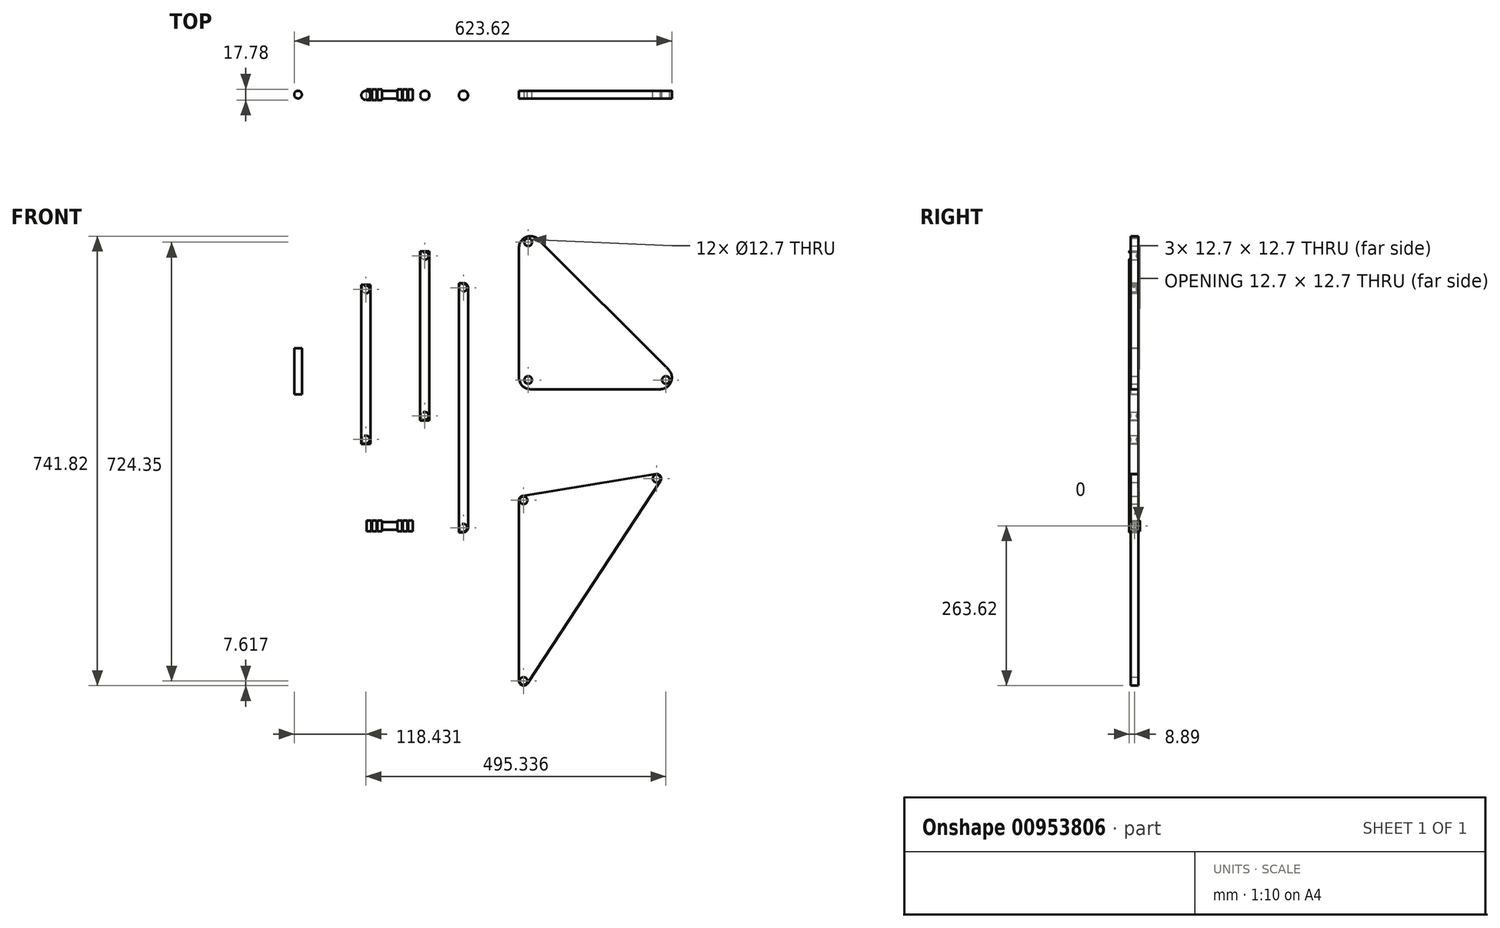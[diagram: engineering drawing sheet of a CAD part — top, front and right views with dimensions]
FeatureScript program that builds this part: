
annotation { "Feature Type Name" : "Feature", "Feature Type Description" : "" }
export const myFeature = defineFeature(function(context is Context, id is Id, definition is map)
    precondition{}
    {
        {
            var Q0;
            Q0=qCreatedBy(makeId("Front.planeOp"),FACE);
            var sketch = newSketch(context, id + "F0", { "sketchPlane" : qUnion([Q0])});
            skLineSegment(sketch, "E0", {"start": v(0, 0) * mm, "end": v(0, 279.4) * mm});
            skLineSegment(sketch, "E1", {"start": v(0, 279.4) * mm, "end": v(279.4, 0) * mm});
            skLineSegment(sketch, "E2", {"start": v(279.4, 0) * mm, "end": v(0, 0) * mm});
            skSolve(sketch);
        }
        {
            var Q0;
            Q0=makeQuery(id+"F0.imprint","IMPRINT",FACE,{"disambiguationData":[TD([[makeQuery(id+"F0.imprint","IMPRINT",EDGE,{"derivedFrom":sQuery(id+"F0.wireOp",EDGE,"E0")}),-1.0]])]});
            extrude(context, id + "F1", {"entities" : qUnion([Q0]), "depth" : 12.7 * mm, "offsetDistance" : 25.4 * mm});
        }
        {
            var Q0;
            Q0=makeQuery(id+"F1.opExtrude","CAP_FACE",FACE,{"disambiguationData":[OSD([sQuery(id+"F0.wireOp",EDGE,"E0"),sQuery(id+"F0.wireOp",EDGE,"E1"),sQuery(id+"F0.wireOp",EDGE,"E2")])],"isStart":true});
            var sketch = newSketch(context, id + "F2", { "sketchPlane" : qUnion([Q0])});
            skPoint(sketch, "E3", {"position": v(-242.6, 15.24) * mm});
            skPoint(sketch, "E4", {"position": v(-15.24, 15.24) * mm});
            skPoint(sketch, "E5", {"position": v(-15.24, 242.6) * mm});
            skLineSegment(sketch, "E6", {"start": v(0, -112.73) * mm, "end": v(-246.38, -112.73) * mm});
            skLineSegment(sketch, "E7", {"start": v(-246.38, -112.73) * mm, "end": v(51.94, -438.82) * mm});
            skLineSegment(sketch, "E8", {"start": v(51.94, -438.82) * mm, "end": v(0, -112.73) * mm});
            skSolve(sketch);
        }
        {
            var Q0;
            Q0=sQuery(id+"F2.wireOp",VERTEX,"E3");
            var Q1;
            Q1=sQuery(id+"F2.wireOp",VERTEX,"E4");
            var Q2;
            Q2=sQuery(id+"F2.wireOp",VERTEX,"E5");
            var Q3;
            Q3=makeQuery(id+"F1.opExtrude","SWEPT_BODY",BODY,{"disambiguationData":[OSD([sQuery(id+"F0.wireOp",EDGE,"E0"),sQuery(id+"F0.wireOp",EDGE,"E1"),sQuery(id+"F0.wireOp",EDGE,"E2")])]});
            hole(context, id + "F3", {"style" : HoleStyle.SIMPLE, "endStyle" : HoleEndStyle.THROUGH, "holeDiameter" : 12.7 * mm, "majorDiameter" : 6.35 * mm, "isTappedThrough" : true, "tappedDepth" : 12.7 * mm, "tapClearance" : 3, "locations" : qUnion([Q0, Q1, Q2]), "scope" : qUnion([Q3])});
        }
        {
            var Q0;
            Q0=makeQuery(id+"F1.opExtrude","SWEPT_EDGE",EDGE,{"disambiguationData":[OSD([sQuery(id+"F0.wireOp",EDGE,"E0"),sQuery(id+"F0.wireOp",EDGE,"E2")])]});
            var Q1;
            Q1=makeQuery(id+"F1.opExtrude","SWEPT_EDGE",EDGE,{"disambiguationData":[OSD([sQuery(id+"F0.wireOp",EDGE,"E0"),sQuery(id+"F0.wireOp",EDGE,"E1")])]});
            var Q2;
            Q2=makeQuery(id+"F1.opExtrude","SWEPT_EDGE",EDGE,{"disambiguationData":[OSD([sQuery(id+"F0.wireOp",EDGE,"E1"),sQuery(id+"F0.wireOp",EDGE,"E2")])]});
            fillet(context, id + "F4", {"entities" : qUnion([Q0, Q1, Q2]), "radius" : 19.05 * mm, "tangentPropagation" : true, "allowEdgeOverflow" : false});
        }
        {
            var Q0;
            Q0=qCreatedBy(makeId("Front.planeOp"),FACE);
            var sketch = newSketch(context, id + "F5", { "sketchPlane" : qUnion([Q0])});
            skLineSegment(sketch, "E9.bottom", {"start": v(-163, 227.77) * mm, "end": v(-147.77, 227.77) * mm});
            skLineSegment(sketch, "E9.top", {"start": v(-163, -51.63) * mm, "end": v(-147.77, -51.63) * mm});
            skLineSegment(sketch, "E9.left", {"start": v(-163, 227.77) * mm, "end": v(-163, -51.63) * mm});
            skLineSegment(sketch, "E9.right", {"start": v(-147.77, 227.77) * mm, "end": v(-147.77, -51.63) * mm});
            skLineSegment(sketch, "E10", {"start": v(-163, 212.53) * mm, "end": v(-147.77, 212.53) * mm, "construction": true});
            skLineSegment(sketch, "E11", {"start": v(-155.39, 227.77) * mm, "end": v(-155.39, 212.53) * mm, "construction": true});
            skLineSegment(sketch, "E12", {"start": v(-155.39, 220.15) * mm, "end": v(-163, 220.15) * mm, "construction": true});
            skLineSegment(sketch, "E13", {"start": v(-155.39, 220.15) * mm, "end": v(-147.77, 220.15) * mm, "construction": true});
            skLineSegment(sketch, "E14", {"start": v(-163, -36.39) * mm, "end": v(-147.77, -36.39) * mm, "construction": true});
            skLineSegment(sketch, "E15", {"start": v(-155.39, -36.39) * mm, "end": v(-155.39, -51.63) * mm, "construction": true});
            skLineSegment(sketch, "E16", {"start": v(-155.39, -44) * mm, "end": v(-147.77, -44) * mm, "construction": true});
            skLineSegment(sketch, "E17", {"start": v(-147.77, -44) * mm, "end": v(-155.39, -44) * mm, "construction": true});
            skLineSegment(sketch, "E18", {"start": v(-163, -44) * mm, "end": v(-155.39, -44) * mm, "construction": true});
            skCircle(sketch, "E19", {"center": v(-155.39, -44) * mm, "radius": 6.35 * mm});
            skCircle(sketch, "E20", {"center": v(-155.39, 220.15) * mm, "radius": 6.35 * mm});
            skSolve(sketch);
        }
        {
            var Q0;
            Q0=makeQuery(id+"F5.imprint","IMPRINT",FACE,{"disambiguationData":[TD([[makeQuery(id+"F5.imprint","IMPRINT",EDGE,{"derivedFrom":sQuery(id+"F5.wireOp",EDGE,"E9.bottom")}),-1.0]])]});
            extrude(context, id + "F6", {"entities" : qUnion([Q0]), "depth" : 15.24 * mm, "offsetDistance" : 25.4 * mm});
        }
        {
            var Q0;
            Q0=makeQuery(id+"F6.opExtrude","CAP_EDGE",EDGE,{"disambiguationData":[OSD([sQuery(id+"F5.wireOp",EDGE,"E9.left")])],"isStart":false});
            var Q1;
            Q1=makeQuery(id+"F6.opExtrude","CAP_EDGE",EDGE,{"disambiguationData":[OSD([sQuery(id+"F5.wireOp",EDGE,"E9.right")])],"isStart":false});
            var Q2;
            Q2=makeQuery(id+"F6.opExtrude","CAP_EDGE",EDGE,{"disambiguationData":[OSD([sQuery(id+"F5.wireOp",EDGE,"E9.right")])],"isStart":true});
            var Q3;
            Q3=makeQuery(id+"F6.opExtrude","CAP_EDGE",EDGE,{"disambiguationData":[OSD([sQuery(id+"F5.wireOp",EDGE,"E9.left")])],"isStart":true});
            fillet(context, id + "F7", {"entities" : qUnion([Q0, Q1, Q2, Q3]), "radius" : 7.62 * mm, "tangentPropagation" : true, "allowEdgeOverflow" : false});
        }
        {
            var Q0;
            Q0=qCreatedBy(makeId("Front.planeOp"),FACE);
            var sketch = newSketch(context, id + "F8", { "sketchPlane" : qUnion([Q0])});
            skLineSegment(sketch, "E21.bottom", {"start": v(-260.35, 172.29) * mm, "end": v(-245.1, 172.29) * mm});
            skLineSegment(sketch, "E21.top", {"start": v(-260.35, -90.6) * mm, "end": v(-245.1, -90.6) * mm});
            skLineSegment(sketch, "E21.left", {"start": v(-260.35, 172.29) * mm, "end": v(-260.35, -90.6) * mm});
            skLineSegment(sketch, "E21.right", {"start": v(-245.1, 172.29) * mm, "end": v(-245.1, -90.6) * mm});
            skLineSegment(sketch, "E22", {"start": v(-260.35, 157.05) * mm, "end": v(-245.1, 157.05) * mm, "construction": true});
            skLineSegment(sketch, "E23", {"start": v(-252.73, 172.29) * mm, "end": v(-252.73, 157.05) * mm, "construction": true});
            skLineSegment(sketch, "E24", {"start": v(-252.73, 157.05) * mm, "end": v(-252.73, 164.67) * mm, "construction": true});
            skLineSegment(sketch, "E25", {"start": v(-252.73, 164.67) * mm, "end": v(-260.35, 164.67) * mm, "construction": true});
            skLineSegment(sketch, "E26", {"start": v(-260.35, 164.67) * mm, "end": v(-252.73, 164.67) * mm, "construction": true});
            skLineSegment(sketch, "E27", {"start": v(-245.1, 164.67) * mm, "end": v(-252.73, 164.67) * mm, "construction": true});
            skLineSegment(sketch, "E28", {"start": v(-260.35, -75.36) * mm, "end": v(-245.1, -75.36) * mm, "construction": true});
            skLineSegment(sketch, "E29", {"start": v(-252.73, -75.36) * mm, "end": v(-252.73, -90.6) * mm, "construction": true});
            skLineSegment(sketch, "E30", {"start": v(-252.73, -90.6) * mm, "end": v(-252.73, -82.98) * mm, "construction": true});
            skLineSegment(sketch, "E31", {"start": v(-252.73, -82.98) * mm, "end": v(-260.35, -82.98) * mm, "construction": true});
            skLineSegment(sketch, "E32", {"start": v(-260.35, -82.98) * mm, "end": v(-252.73, -82.98) * mm, "construction": true});
            skLineSegment(sketch, "E33", {"start": v(-245.1, -82.98) * mm, "end": v(-252.73, -82.98) * mm, "construction": true});
            skCircle(sketch, "E34", {"center": v(-252.73, -82.98) * mm, "radius": 6.35 * mm});
            skCircle(sketch, "E35", {"center": v(-252.73, 164.67) * mm, "radius": 6.35 * mm});
            skSolve(sketch);
        }
        {
            var Q0;
            Q0=makeQuery(id+"F8.imprint","IMPRINT",FACE,{"disambiguationData":[TD([[makeQuery(id+"F8.imprint","IMPRINT",EDGE,{"derivedFrom":sQuery(id+"F8.wireOp",EDGE,"E21.bottom")}),-1.0]])]});
            extrude(context, id + "F9", {"entities" : qUnion([Q0]), "depth" : 15.24 * mm, "offsetDistance" : 25.4 * mm});
        }
        {
            var Q0;
            Q0=makeQuery(id+"F9.opExtrude","CAP_EDGE",EDGE,{"disambiguationData":[OSD([sQuery(id+"F8.wireOp",EDGE,"E21.left")])],"isStart":false});
            var Q1;
            Q1=makeQuery(id+"F9.opExtrude","CAP_EDGE",EDGE,{"disambiguationData":[OSD([sQuery(id+"F8.wireOp",EDGE,"E21.right")])],"isStart":false});
            var Q2;
            Q2=makeQuery(id+"F9.opExtrude","CAP_EDGE",EDGE,{"disambiguationData":[OSD([sQuery(id+"F8.wireOp",EDGE,"E21.left")])],"isStart":true});
            var Q3;
            Q3=makeQuery(id+"F9.opExtrude","CAP_EDGE",EDGE,{"disambiguationData":[OSD([sQuery(id+"F8.wireOp",EDGE,"E21.right")])],"isStart":true});
            fillet(context, id + "F10", {"entities" : qUnion([Q0, Q1, Q2, Q3]), "radius" : 7.62 * mm, "tangentPropagation" : true, "allowEdgeOverflow" : false});
        }
        {
            var Q0;
            Q0=qCreatedBy(makeId("Front.planeOp"),FACE);
            var sketch = newSketch(context, id + "F11", { "sketchPlane" : qUnion([Q0])});
            skLineSegment(sketch, "E36", {"start": v(0, -177.01) * mm, "end": v(0, -507.21) * mm});
            skLineSegment(sketch, "E37", {"start": v(0, -507.21) * mm, "end": v(243.15, -137.24) * mm});
            skLineSegment(sketch, "E38", {"start": v(243.15, -137.24) * mm, "end": v(0, -177.01) * mm});
            skPoint(sketch, "E39", {"position": v(7.62, -183.49) * mm});
            skPoint(sketch, "E40", {"position": v(227.25, -147.56) * mm});
            skCircle(sketch, "E41", {"center": v(7.62, -183.49) * mm, "radius": 6.35 * mm});
            skCircle(sketch, "E42", {"center": v(227.25, -147.56) * mm, "radius": 6.35 * mm});
            skPoint(sketch, "E43", {"position": v(7.62, -481.74) * mm});
            skCircle(sketch, "E44", {"center": v(7.62, -481.74) * mm, "radius": 6.35 * mm});
            skSolve(sketch);
        }
        {
            var Q0;
            Q0=makeQuery(id+"F11.imprint","IMPRINT",FACE,{"disambiguationData":[TD([[makeQuery(id+"F11.imprint","IMPRINT",EDGE,{"derivedFrom":sQuery(id+"F11.wireOp",EDGE,"E36")}),1.0]])]});
            extrude(context, id + "F12", {"entities" : qUnion([Q0]), "depth" : 12.7 * mm, "offsetDistance" : 25.4 * mm});
        }
        {
            var Q0;
            Q0=makeQuery(id+"F12.opExtrude","SWEPT_EDGE",EDGE,{"disambiguationData":[OSD([sQuery(id+"F11.wireOp",EDGE,"E37"),sQuery(id+"F11.wireOp",EDGE,"E38")])]});
            var Q1;
            Q1=makeQuery(id+"F12.opExtrude","SWEPT_EDGE",EDGE,{"disambiguationData":[OSD([sQuery(id+"F11.wireOp",EDGE,"E36"),sQuery(id+"F11.wireOp",EDGE,"E37")])]});
            var Q2;
            Q2=makeQuery(id+"F12.opExtrude","SWEPT_EDGE",EDGE,{"disambiguationData":[OSD([sQuery(id+"F11.wireOp",EDGE,"E36"),sQuery(id+"F11.wireOp",EDGE,"E38")])]});
            fillet(context, id + "F13", {"entities" : qUnion([Q0, Q1, Q2]), "radius" : 7.62 * mm, "tangentPropagation" : true, "allowEdgeOverflow" : false});
        }
        {
            var Q0;
            Q0=qCreatedBy(makeId("Front.planeOp"),FACE);
            var sketch = newSketch(context, id + "F14", { "sketchPlane" : qUnion([Q0])});
            skLineSegment(sketch, "E45.bottom", {"start": v(-251.68, -219.4) * mm, "end": v(-175.48, -219.4) * mm});
            skLineSegment(sketch, "E45.top", {"start": v(-251.68, -232.1) * mm, "end": v(-175.48, -232.1) * mm});
            skLineSegment(sketch, "E45.left", {"start": v(-251.68, -219.4) * mm, "end": v(-251.68, -232.1) * mm});
            skLineSegment(sketch, "E45.right", {"start": v(-175.48, -219.4) * mm, "end": v(-175.48, -232.1) * mm});
            skSolve(sketch);
        }
        {
            var Q0;
            Q0=makeQuery(id+"F14.imprint","IMPRINT",FACE,{"disambiguationData":[TD([[makeQuery(id+"F14.imprint","IMPRINT",EDGE,{"derivedFrom":sQuery(id+"F14.wireOp",EDGE,"E45.bottom")}),-1.0]])]});
            extrude(context, id + "F15", {"entities" : qUnion([Q0]), "depth" : 12.7 * mm, "offsetDistance" : 25.4 * mm});
        }
        {
            var Q0;
            Q0=makeQuery(id+"F15.opExtrude","CAP_FACE",FACE,{"disambiguationData":[OSD([sQuery(id+"F14.wireOp",EDGE,"E45.bottom"),sQuery(id+"F14.wireOp",EDGE,"E45.top"),sQuery(id+"F14.wireOp",EDGE,"E45.left"),sQuery(id+"F14.wireOp",EDGE,"E45.right")])],"isStart":false});
            var sketch = newSketch(context, id + "F16", { "sketchPlane" : qUnion([Q0])});
            skLineSegment(sketch, "E46", {"start": v(-213.58, -219.4) * mm, "end": v(-213.58, -232.1) * mm});
            skLineSegment(sketch, "E47", {"start": v(-226.28, -219.4) * mm, "end": v(-226.28, -232.1) * mm});
            skLineSegment(sketch, "E48", {"start": v(-200.88, -232.1) * mm, "end": v(-200.88, -219.4) * mm});
            skLineSegment(sketch, "E49.bottom", {"start": v(-193.26, -219.4) * mm, "end": v(-191.99, -219.4) * mm});
            skLineSegment(sketch, "E49.top", {"start": v(-193.26, -232.1) * mm, "end": v(-191.99, -232.1) * mm});
            skLineSegment(sketch, "E49.left", {"start": v(-193.26, -219.4) * mm, "end": v(-193.26, -232.1) * mm});
            skLineSegment(sketch, "E49.right", {"start": v(-191.99, -219.4) * mm, "end": v(-191.99, -232.1) * mm});
            skLineSegment(sketch, "E50.bottom", {"start": v(-184.37, -219.4) * mm, "end": v(-183.1, -219.4) * mm});
            skLineSegment(sketch, "E50.top", {"start": v(-184.37, -232.1) * mm, "end": v(-183.1, -232.1) * mm});
            skLineSegment(sketch, "E50.left", {"start": v(-184.37, -219.4) * mm, "end": v(-184.37, -232.1) * mm});
            skLineSegment(sketch, "E50.right", {"start": v(-183.1, -219.4) * mm, "end": v(-183.1, -232.1) * mm});
            skLineSegment(sketch, "E51.bottom", {"start": v(-244.06, -219.4) * mm, "end": v(-242.79, -219.4) * mm});
            skLineSegment(sketch, "E51.top", {"start": v(-244.06, -232.1) * mm, "end": v(-242.79, -232.1) * mm});
            skLineSegment(sketch, "E51.left", {"start": v(-244.06, -219.4) * mm, "end": v(-244.06, -232.1) * mm});
            skLineSegment(sketch, "E51.right", {"start": v(-242.79, -219.4) * mm, "end": v(-242.79, -232.1) * mm});
            skLineSegment(sketch, "E52.bottom", {"start": v(-235.17, -219.4) * mm, "end": v(-233.9, -219.4) * mm});
            skLineSegment(sketch, "E52.top", {"start": v(-235.17, -232.1) * mm, "end": v(-233.9, -232.1) * mm});
            skLineSegment(sketch, "E52.left", {"start": v(-235.17, -219.4) * mm, "end": v(-235.17, -232.1) * mm});
            skLineSegment(sketch, "E52.right", {"start": v(-233.9, -219.4) * mm, "end": v(-233.9, -232.1) * mm});
            skSolve(sketch);
        }
        {
            var Q0;
            {var subQ0=sQuery(id+"F16.wireOp",EDGE,"E51.left");Q0=makeQuery(id+"F16.imprint","IMPRINT",FACE,{"disambiguationData":[TD([[makeQuery(id+"F16.imprint","IMPRINT",EDGE,{"derivedFrom":subQ0}),-1.0]])]});}
            var Q1;
            {var subQ0=sQuery(id+"F16.wireOp",EDGE,"E51.right");Q1=makeQuery(id+"F16.imprint","IMPRINT",FACE,{"disambiguationData":[TD([[makeQuery(id+"F16.imprint","IMPRINT",EDGE,{"derivedFrom":subQ0}),1.0]])]});}
            var Q2;
            {var subQ0=sQuery(id+"F16.wireOp",EDGE,"E47");Q2=makeQuery(id+"F16.imprint","IMPRINT",FACE,{"disambiguationData":[TD([[makeQuery(id+"F16.imprint","IMPRINT",EDGE,{"derivedFrom":subQ0}),-1.0]])]});}
            var Q3;
            {var subQ0=sQuery(id+"F16.wireOp",EDGE,"E48");Q3=makeQuery(id+"F16.imprint","IMPRINT",FACE,{"disambiguationData":[TD([[makeQuery(id+"F16.imprint","IMPRINT",EDGE,{"derivedFrom":subQ0}),-1.0]])]});}
            var Q4;
            {var subQ0=sQuery(id+"F16.wireOp",EDGE,"E49.right");Q4=makeQuery(id+"F16.imprint","IMPRINT",FACE,{"disambiguationData":[TD([[makeQuery(id+"F16.imprint","IMPRINT",EDGE,{"derivedFrom":subQ0}),1.0]])]});}
            var Q5;
            {var subQ0=sQuery(id+"F16.wireOp",EDGE,"E50.right");Q5=makeQuery(id+"F16.imprint","IMPRINT",FACE,{"disambiguationData":[TD([[makeQuery(id+"F16.imprint","IMPRINT",EDGE,{"derivedFrom":subQ0}),1.0]])]});}
            extrude(context, id + "F17", {"entities" : qUnion([Q0, Q1, Q2, Q3, Q4, Q5]), "operationType" : NewBodyOperationType.ADD, "depth" : 2.54 * mm, "offsetDistance" : 25.4 * mm, "hasSecondDirection" : true, "secondDirectionOppositeDirection" : true, "secondDirectionDepth" : 15.24 * mm});
        }
        {
            var Q0;
            {var subQ0=sQuery(id+"F16.wireOp",EDGE,"E51.bottom");var subQ1=sQuery(id+"F14.wireOp",EDGE,"E45.bottom");var subQ2=makeQuery(id+"F15.opExtrude","CAP_EDGE",EDGE,{"disambiguationData":[OSD([subQ1])],"isStart":false});var subQ4=sQuery(id+"F16.wireOp",EDGE,"E49.bottom");Q0=makeQuery(id+"F17.boolean.opBoolean","MERGE",FACE,{"derivedFrom":[makeQuery(id+"F15.opExtrude","SWEPT_FACE",FACE,{"disambiguationData":[OSD([subQ1])]}),makeQuery(id+"F17.opExtrude","SWEPT_FACE",FACE,{"disambiguationData":[OSD([subQ1]),TDD([makeQuery(id+"F16.imprint","IMPRINT",EDGE,{"disambiguationData":[TD([[makeQuery(id+"F16.imprint","INTERSECT",VERTEX,{"derivedFrom":[subQ2,makeQuery(id+"F15.opExtrude","CAP_EDGE",EDGE,{"disambiguationData":[OSD([sQuery(id+"F14.wireOp",EDGE,"E45.left")])],"isStart":false})]}),-1.0]])],"derivedFrom":subQ2})])]}),makeQuery(id+"F17.opExtrude","SWEPT_FACE",FACE,{"disambiguationData":[OSD([subQ1]),TDD([makeQuery(id+"F16.imprint","IMPRINT",EDGE,{"disambiguationData":[TD([[makeQuery(id+"F16.imprint","INTERSECT",VERTEX,{"derivedFrom":[subQ2,makeQuery(id+"F15.opExtrude","CAP_EDGE",EDGE,{"disambiguationData":[OSD([sQuery(id+"F14.wireOp",EDGE,"E45.right")])],"isStart":false})]}),1.0]])],"derivedFrom":subQ2})])]}),makeQuery(id+"F17.opExtrude","SWEPT_FACE",FACE,{"disambiguationData":[OSD([subQ1]),TDD([makeQuery(id+"F16.imprint","IMPRINT",EDGE,{"disambiguationData":[TD([[makeQuery(id+"F16.imprint","INTERSECT",VERTEX,{"derivedFrom":[subQ2,sQuery(id+"F16.wireOp",EDGE,"E47")]}),1.0]])],"derivedFrom":subQ2})])]}),makeQuery(id+"F17.opExtrude","SWEPT_FACE",FACE,{"disambiguationData":[OSD([subQ1]),TDD([makeQuery(id+"F16.imprint","IMPRINT",EDGE,{"disambiguationData":[TD([[makeQuery(id+"F16.imprint","INTERSECT",VERTEX,{"derivedFrom":[subQ2,sQuery(id+"F16.wireOp",EDGE,"E48")]}),-1.0]])],"derivedFrom":subQ2})])]}),makeQuery(id+"F17.opExtrude","SWEPT_FACE",FACE,{"disambiguationData":[OSD([subQ1]),TDD([makeQuery(id+"F16.imprint","IMPRINT",EDGE,{"disambiguationData":[TD([[makeQuery(id+"F16.imprint","INTERSECT",VERTEX,{"derivedFrom":[subQ2,subQ4,sQuery(id+"F16.wireOp",EDGE,"E49.right")]}),-1.0]])],"derivedFrom":subQ2})])]}),makeQuery(id+"F17.opExtrude","SWEPT_FACE",FACE,{"disambiguationData":[OSD([subQ1]),TDD([makeQuery(id+"F16.imprint","IMPRINT",EDGE,{"disambiguationData":[TD([[makeQuery(id+"F16.imprint","INTERSECT",VERTEX,{"derivedFrom":[subQ2,subQ0,sQuery(id+"F16.wireOp",EDGE,"E51.right")]}),-1.0]])],"derivedFrom":subQ2})])]})]});}
            var sketch = newSketch(context, id + "F18", { "sketchPlane" : qUnion([Q0])});
            skLineSegment(sketch, "E53.bottom", {"start": v(-244.06, 0) * mm, "end": v(-242.79, 0) * mm});
            skLineSegment(sketch, "E53.top", {"start": v(-244.06, -12.7) * mm, "end": v(-242.79, -12.7) * mm});
            skLineSegment(sketch, "E53.left", {"start": v(-244.06, 0) * mm, "end": v(-244.06, -12.7) * mm});
            skLineSegment(sketch, "E53.right", {"start": v(-242.79, 0) * mm, "end": v(-242.79, -12.7) * mm});
            skLineSegment(sketch, "E54.bottom", {"start": v(-235.17, 0) * mm, "end": v(-233.9, 0) * mm});
            skLineSegment(sketch, "E54.top", {"start": v(-235.17, -12.7) * mm, "end": v(-233.9, -12.7) * mm});
            skLineSegment(sketch, "E54.left", {"start": v(-235.17, 0) * mm, "end": v(-235.17, -12.7) * mm});
            skLineSegment(sketch, "E54.right", {"start": v(-233.9, 0) * mm, "end": v(-233.9, -12.7) * mm});
            skLineSegment(sketch, "E55.bottom", {"start": v(-193.26, 0) * mm, "end": v(-191.99, 0) * mm});
            skLineSegment(sketch, "E55.top", {"start": v(-193.26, -12.7) * mm, "end": v(-191.99, -12.7) * mm});
            skLineSegment(sketch, "E55.left", {"start": v(-193.26, 0) * mm, "end": v(-193.26, -12.7) * mm});
            skLineSegment(sketch, "E55.right", {"start": v(-191.99, 0) * mm, "end": v(-191.99, -12.7) * mm});
            skLineSegment(sketch, "E56.bottom", {"start": v(-184.37, 0) * mm, "end": v(-183.1, 0) * mm});
            skLineSegment(sketch, "E56.top", {"start": v(-184.37, -12.7) * mm, "end": v(-183.1, -12.7) * mm});
            skLineSegment(sketch, "E56.left", {"start": v(-184.37, 0) * mm, "end": v(-184.37, -12.7) * mm});
            skLineSegment(sketch, "E56.right", {"start": v(-183.1, 0) * mm, "end": v(-183.1, -12.7) * mm});
            skLineSegment(sketch, "E57", {"start": v(-200.88, 0) * mm, "end": v(-200.88, -12.7) * mm});
            skLineSegment(sketch, "E58", {"start": v(-226.28, 0) * mm, "end": v(-226.28, -12.7) * mm});
            skSolve(sketch);
        }
        {
            var Q0;
            Q0=makeQuery(id+"F18.imprint","IMPRINT",FACE,{"disambiguationData":[TD([[makeQuery(id+"F18.imprint","IMPRINT",EDGE,{"derivedFrom":sQuery(id+"F18.wireOp",EDGE,"E53.left")}),-1.0]])]});
            var Q1;
            Q1=makeQuery(id+"F18.imprint","IMPRINT",FACE,{"disambiguationData":[TD([[makeQuery(id+"F18.imprint","IMPRINT",EDGE,{"derivedFrom":sQuery(id+"F18.wireOp",EDGE,"E53.right")}),1.0]])]});
            var Q2;
            Q2=makeQuery(id+"F18.imprint","IMPRINT",FACE,{"disambiguationData":[TD([[makeQuery(id+"F18.imprint","IMPRINT",EDGE,{"derivedFrom":sQuery(id+"F18.wireOp",EDGE,"E54.right")}),1.0]])]});
            var Q3;
            Q3=makeQuery(id+"F18.imprint","IMPRINT",FACE,{"disambiguationData":[TD([[makeQuery(id+"F18.imprint","IMPRINT",EDGE,{"derivedFrom":sQuery(id+"F18.wireOp",EDGE,"E55.left")}),-1.0]])]});
            var Q4;
            Q4=makeQuery(id+"F18.imprint","IMPRINT",FACE,{"disambiguationData":[TD([[makeQuery(id+"F18.imprint","IMPRINT",EDGE,{"derivedFrom":sQuery(id+"F18.wireOp",EDGE,"E55.right")}),1.0]])]});
            var Q5;
            Q5=makeQuery(id+"F18.imprint","IMPRINT",FACE,{"disambiguationData":[TD([[makeQuery(id+"F18.imprint","IMPRINT",EDGE,{"derivedFrom":sQuery(id+"F18.wireOp",EDGE,"E56.right")}),1.0]])]});
            extrude(context, id + "F19", {"entities" : qUnion([Q0, Q1, Q2, Q3, Q4, Q5]), "operationType" : NewBodyOperationType.ADD, "depth" : 2.54 * mm, "offsetDistance" : 25.4 * mm, "hasSecondDirection" : true, "secondDirectionOppositeDirection" : true, "secondDirectionDepth" : 15.24 * mm});
        }
        {
            var Q0;
            {var subQ2=sQuery(id+"F14.wireOp",EDGE,"E45.bottom");var subQ3=makeQuery(id+"F15.opExtrude","CAP_EDGE",EDGE,{"disambiguationData":[OSD([subQ2])],"isStart":false});var subQ5=sQuery(id+"F16.wireOp",EDGE,"E47");Q0=makeQuery(id+"F17.boolean.opBoolean","SPLIT",EDGE,{"disambiguationData":[TD([makeQuery(id+"F17.opExtrude","SWEPT_FACE",FACE,{"disambiguationData":[OSD([subQ5])]})])],"derivedFrom":subQ3});}
            var Q1;
            {var subQ1=sQuery(id+"F16.wireOp",EDGE,"E47");var subQ2=sQuery(id+"F14.wireOp",EDGE,"E45.top");var subQ3=makeQuery(id+"F15.opExtrude","CAP_EDGE",EDGE,{"disambiguationData":[OSD([subQ2])],"isStart":false});Q1=makeQuery(id+"F17.boolean.opBoolean","SPLIT",EDGE,{"disambiguationData":[TD([makeQuery(id+"F17.opExtrude","SWEPT_FACE",FACE,{"disambiguationData":[OSD([subQ1])]})])],"derivedFrom":subQ3});}
            var Q2;
            {var subQ0=sQuery(id+"F16.wireOp",EDGE,"E47");var subQ3=sQuery(id+"F14.wireOp",EDGE,"E45.top");Q2=makeQuery(id+"F17.boolean.opBoolean","SPLIT",EDGE,{"disambiguationData":[TD([makeQuery(id+"F17.opExtrude","SWEPT_FACE",FACE,{"disambiguationData":[OSD([subQ0])]})])],"derivedFrom":makeQuery(id+"F15.opExtrude","CAP_EDGE",EDGE,{"disambiguationData":[OSD([subQ3])],"isStart":true})});}
            var Q3;
            {var subQ0=sQuery(id+"F16.wireOp",EDGE,"E47");var subQ3=sQuery(id+"F14.wireOp",EDGE,"E45.bottom");Q3=makeQuery(id+"F17.boolean.opBoolean","SPLIT",EDGE,{"disambiguationData":[TD([makeQuery(id+"F17.opExtrude","SWEPT_FACE",FACE,{"disambiguationData":[OSD([subQ0])]})])],"derivedFrom":makeQuery(id+"F15.opExtrude","CAP_EDGE",EDGE,{"disambiguationData":[OSD([subQ3])],"isStart":true})});}
            fillet(context, id + "F20", {"entities" : qUnion([Q0, Q1, Q2, Q3]), "radius" : 6.35 * mm, "tangentPropagation" : true, "allowEdgeOverflow" : false});
        }
        {
            var Q0;
            Q0=qCreatedBy(makeId("Front.planeOp"),FACE);
            var sketch = newSketch(context, id + "F21", { "sketchPlane" : qUnion([Q0])});
            skLineSegment(sketch, "E59.bottom", {"start": v(-371.16, 67.4) * mm, "end": v(-358.46, 67.4) * mm});
            skLineSegment(sketch, "E59.top", {"start": v(-371.16, -8.8) * mm, "end": v(-358.46, -8.8) * mm});
            skLineSegment(sketch, "E59.left", {"start": v(-371.16, 67.4) * mm, "end": v(-371.16, -8.8) * mm});
            skLineSegment(sketch, "E59.right", {"start": v(-358.46, 67.4) * mm, "end": v(-358.46, -8.8) * mm});
            skSolve(sketch);
        }
        {
            var Q0;
            Q0=makeQuery(id+"F21.imprint","IMPRINT",FACE,{"disambiguationData":[TD([[makeQuery(id+"F21.imprint","IMPRINT",EDGE,{"derivedFrom":sQuery(id+"F21.wireOp",EDGE,"E59.bottom")}),-1.0]])]});
            extrude(context, id + "F22", {"entities" : qUnion([Q0]), "depth" : 12.7 * mm, "offsetDistance" : 25.4 * mm});
        }
        {
            var Q0;
            Q0=makeQuery(id+"F22.opExtrude","CAP_EDGE",EDGE,{"disambiguationData":[OSD([sQuery(id+"F21.wireOp",EDGE,"E59.left")])],"isStart":false});
            var Q1;
            Q1=makeQuery(id+"F22.opExtrude","CAP_EDGE",EDGE,{"disambiguationData":[OSD([sQuery(id+"F21.wireOp",EDGE,"E59.right")])],"isStart":false});
            var Q2;
            Q2=makeQuery(id+"F22.opExtrude","CAP_EDGE",EDGE,{"disambiguationData":[OSD([sQuery(id+"F21.wireOp",EDGE,"E59.right")])],"isStart":true});
            var Q3;
            Q3=makeQuery(id+"F22.opExtrude","CAP_EDGE",EDGE,{"disambiguationData":[OSD([sQuery(id+"F21.wireOp",EDGE,"E59.left")])],"isStart":true});
            fillet(context, id + "F23", {"entities" : qUnion([Q0, Q1, Q2, Q3]), "radius" : 6.35 * mm, "tangentPropagation" : true, "allowEdgeOverflow" : false});
        }
        {
            var Q0;
            Q0=qCreatedBy(makeId("Front.planeOp"),FACE);
            var sketch = newSketch(context, id + "F24", { "sketchPlane" : qUnion([Q0])});
            skLineSegment(sketch, "E60.bottom", {"start": v(-99.33, 175.18) * mm, "end": v(-84.09, 175.18) * mm});
            skLineSegment(sketch, "E60.top", {"start": v(-99.33, -236.3) * mm, "end": v(-84.09, -236.3) * mm});
            skLineSegment(sketch, "E60.left", {"start": v(-99.33, 175.18) * mm, "end": v(-99.33, -236.3) * mm});
            skLineSegment(sketch, "E60.right", {"start": v(-84.09, 175.18) * mm, "end": v(-84.09, -236.3) * mm});
            skLineSegment(sketch, "E61", {"start": v(-99.33, 159.94) * mm, "end": v(-84.09, 159.94) * mm, "construction": true});
            skLineSegment(sketch, "E62", {"start": v(-91.7, 175.18) * mm, "end": v(-91.7, 159.94) * mm, "construction": true});
            skLineSegment(sketch, "E63", {"start": v(-91.7, 159.94) * mm, "end": v(-91.7, 167.56) * mm, "construction": true});
            skLineSegment(sketch, "E64", {"start": v(-91.7, 167.56) * mm, "end": v(-84.09, 167.56) * mm, "construction": true});
            skLineSegment(sketch, "E65", {"start": v(-84.09, 167.56) * mm, "end": v(-99.33, 167.56) * mm, "construction": true});
            skPoint(sketch, "E66", {"position": v(-91.7, 167.56) * mm});
            skLineSegment(sketch, "E67.bottom", {"start": v(-84.09, -236.3) * mm, "end": v(-99.33, -236.3) * mm, "construction": true});
            skLineSegment(sketch, "E67.top", {"start": v(-84.09, -221.06) * mm, "end": v(-99.33, -221.06) * mm, "construction": true});
            skLineSegment(sketch, "E67.left", {"start": v(-84.09, -236.3) * mm, "end": v(-84.09, -221.06) * mm, "construction": true});
            skLineSegment(sketch, "E67.right", {"start": v(-99.33, -236.3) * mm, "end": v(-99.33, -221.06) * mm, "construction": true});
            skPoint(sketch, "E67.middle", {"position": v(-91.7, -228.68) * mm});
            skSolve(sketch);
        }
        {
            var Q0;
            Q0=makeQuery(id+"F24.imprint","IMPRINT",FACE,{"disambiguationData":[TD([[makeQuery(id+"F24.imprint","IMPRINT",EDGE,{"derivedFrom":sQuery(id+"F24.wireOp",EDGE,"E60.bottom")}),-1.0]])]});
            extrude(context, id + "F25", {"entities" : qUnion([Q0]), "depth" : 15.24 * mm, "offsetDistance" : 25.4 * mm});
        }
        {
            var Q0;
            Q0=sQuery(id+"F24.wireOp",VERTEX,"E66");
            var Q1;
            Q1=sQuery(id+"F24.wireOp",VERTEX,"E67.middle");
            var Q2;
            Q2=makeQuery(id+"F25.opExtrude","SWEPT_BODY",BODY,{"disambiguationData":[OSD([sQuery(id+"F24.wireOp",EDGE,"E60.bottom"),sQuery(id+"F24.wireOp",EDGE,"E60.top"),sQuery(id+"F24.wireOp",EDGE,"E60.left"),sQuery(id+"F24.wireOp",EDGE,"E60.right")])]});
            hole(context, id + "F26", {"style" : HoleStyle.SIMPLE, "endStyle" : HoleEndStyle.THROUGH, "oppositeDirection" : true, "holeDiameter" : 12.7 * mm, "majorDiameter" : 6.35 * mm, "isTappedThrough" : true, "tappedDepth" : 12.7 * mm, "tapClearance" : 3, "locations" : qUnion([Q0, Q1]), "scope" : qUnion([Q2])});
        }
        {
            var Q0;
            Q0=makeQuery(id+"F25.opExtrude","CAP_EDGE",EDGE,{"disambiguationData":[OSD([sQuery(id+"F24.wireOp",EDGE,"E60.left")])],"isStart":true});
            var Q1;
            Q1=makeQuery(id+"F25.opExtrude","CAP_EDGE",EDGE,{"disambiguationData":[OSD([sQuery(id+"F24.wireOp",EDGE,"E60.left")])],"isStart":false});
            var Q2;
            Q2=makeQuery(id+"F25.opExtrude","CAP_EDGE",EDGE,{"disambiguationData":[OSD([sQuery(id+"F24.wireOp",EDGE,"E60.right")])],"isStart":false});
            var Q3;
            Q3=makeQuery(id+"F25.opExtrude","SWEPT_FACE",FACE,{"disambiguationData":[OSD([sQuery(id+"F24.wireOp",EDGE,"E60.right")])]});
            fillet(context, id + "F27", {"entities" : qUnion([Q0, Q1, Q2, Q3]), "radius" : 7.62 * mm, "tangentPropagation" : true, "allowEdgeOverflow" : false});
        }
    });
